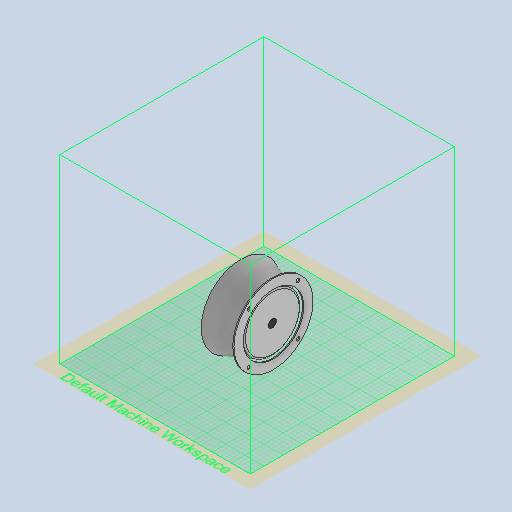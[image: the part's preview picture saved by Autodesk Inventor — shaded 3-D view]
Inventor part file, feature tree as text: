
AUTODESK INVENTOR PART (.ipt)
format: ipt  version: 2022 (Build 260153000, 153)  size: 496,640 bytes
history: mixed  units: in
note: dims shown in document units (in); Inventor stores cm internally (conversion verified against a paired STEP export)
features: thicken_offset x1, extrude x1, mirror x1, sketch x1, imported_body x1
ambient origin geometry x8: Origin, YZ Plane, XZ Plane, XY Plane, X Axis, Y Axis, Z Axis, Center Point
bodies: Solid1 (imported_parasolid), Body1 (imported_parasolid)
feature tree (5):
  thicken_offset  "Thicken1"
  extrude  "Extrusion3"  Depth=0.472in
  mirror  "Mirror1"
  sketch  "Sketch3"  dims[d6=0.472in d7=0.472in d13=1.1811in d14=0.0in d4=0.0197in d5=1.9685in d15=0.0197in d16=1.9685in d17=0.0197in d18=1.9685in]
  imported_body  NMx_Import_Brep_tag  [imported B-rep: ~6 faces, bbox_mm=None]
